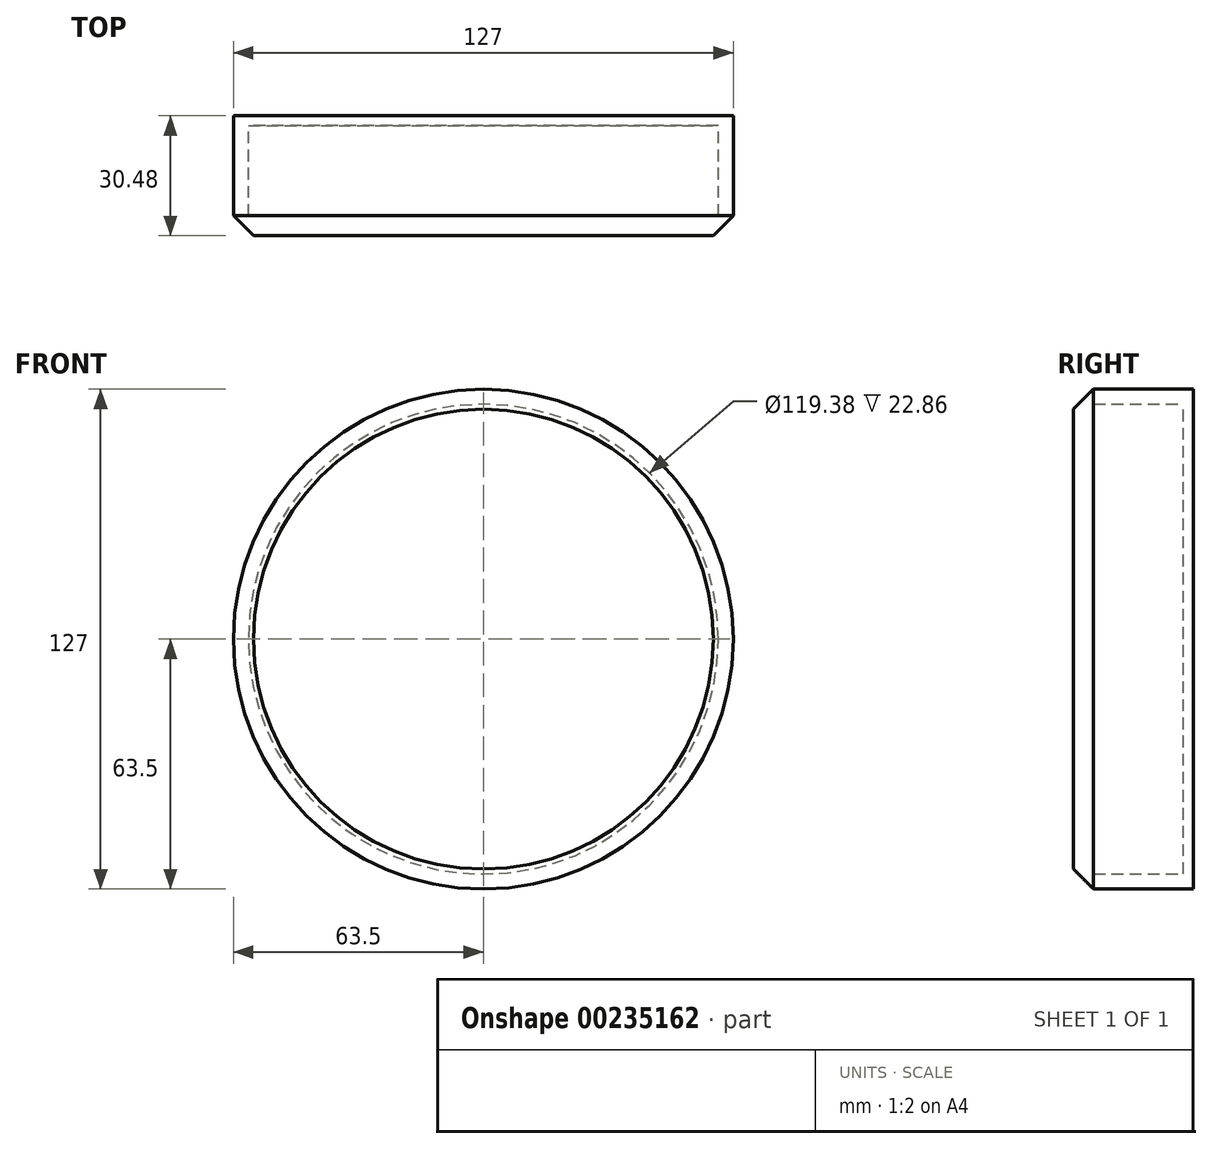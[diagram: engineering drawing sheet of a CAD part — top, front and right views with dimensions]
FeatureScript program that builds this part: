
annotation { "Feature Type Name" : "Feature", "Feature Type Description" : "" }
export const myFeature = defineFeature(function(context is Context, id is Id, definition is map)
    precondition{}
    {
        {
            var Q0;
            Q0=qCreatedBy(makeId("Front.planeOp"),FACE);
            var sketch = newSketch(context, id + "F0", { "sketchPlane" : qUnion([Q0])});
            skCircle(sketch, "E0", {"center": v(0, 0) * mm, "radius": 63.5 * mm});
            skCircle(sketch, "E1", {"center": v(0, 0) * mm, "radius": 62.23 * mm});
            skSolve(sketch);
        }
        {
            var Q0;
            Q0=makeQuery(id+"F0.imprint","IMPRINT",FACE,{"disambiguationData":[TD([[makeQuery(id+"F0.imprint","IMPRINT",EDGE,{"derivedFrom":sQuery(id+"F0.wireOp",EDGE,"E1")}),1.0]])]});
            extrude(context, id + "F5", {"entities" : qUnion([Q0]), "depth" : 25.4 * mm});
        }
        {
            var Q0;
            Q0=makeQuery(id+"F5.opExtrude","CAP_FACE",FACE,{"disambiguationData":[OSD([sQuery(id+"F0.wireOp",EDGE,"E1")])],"isStart":false});
            shell(context, id + "F1", {"entities" : qUnion([Q0]), "thickness" : 2.54 * mm});
        }
        {
            var Q0;
            Q0=makeQuery(id+"F0.imprint","IMPRINT",FACE,{"disambiguationData":[TD([[makeQuery(id+"F0.imprint","IMPRINT",EDGE,{"derivedFrom":sQuery(id+"F0.wireOp",EDGE,"E0")}),1.0]])]});
            extrude(context, id + "F6", {"entities" : qUnion([Q0]), "operationType" : NewBodyOperationType.ADD, "depth" : 12.7 * mm});
        }
        {
            var Q0;
            Q0=makeQuery(id+"F6.opExtrude","CAP_FACE",FACE,{"disambiguationData":[OSD([sQuery(id+"F0.wireOp",EDGE,"E0"),sQuery(id+"F0.wireOp",EDGE,"E1")])],"isStart":false});
            extrude(context, id + "F2", {"entities" : qUnion([Q0]), "depth" : 12.7 * mm});
        }
        {
            var Q0;
            Q0=makeQuery(id+"F2.opExtrude","CAP_FACE",FACE,{"disambiguationData":[OSD([sQuery(id+"F0.wireOp",EDGE,"E0"),sQuery(id+"F0.wireOp",EDGE,"E1")])],"isStart":false});
            var sketch = newSketch(context, id + "F7", { "sketchPlane" : qUnion([Q0])});
            skCircle(sketch, "E2", {"center": v(0, 0) * mm, "radius": 63.5 * mm});
            skSolve(sketch);
        }
        {
            var Q0;
            Q0 = qSketchRegion(id + "F7", true);
            extrude(context, id + "F3", {"entities" : qUnion([Q0]), "operationType" : NewBodyOperationType.ADD, "depth" : 5.08 * mm});
        }
        {
            var Q0;
            Q0=makeQuery(id+"F3.opExtrude","CAP_EDGE",EDGE,{"disambiguationData":[OSD([sQuery(id+"F7.wireOp",EDGE,"E2")])],"isStart":false});
            chamfer(context, id + "F4", {"entities" : qUnion([Q0]), "width" : 5.08 * mm, "tangentPropagation" : true});
        }
    });
